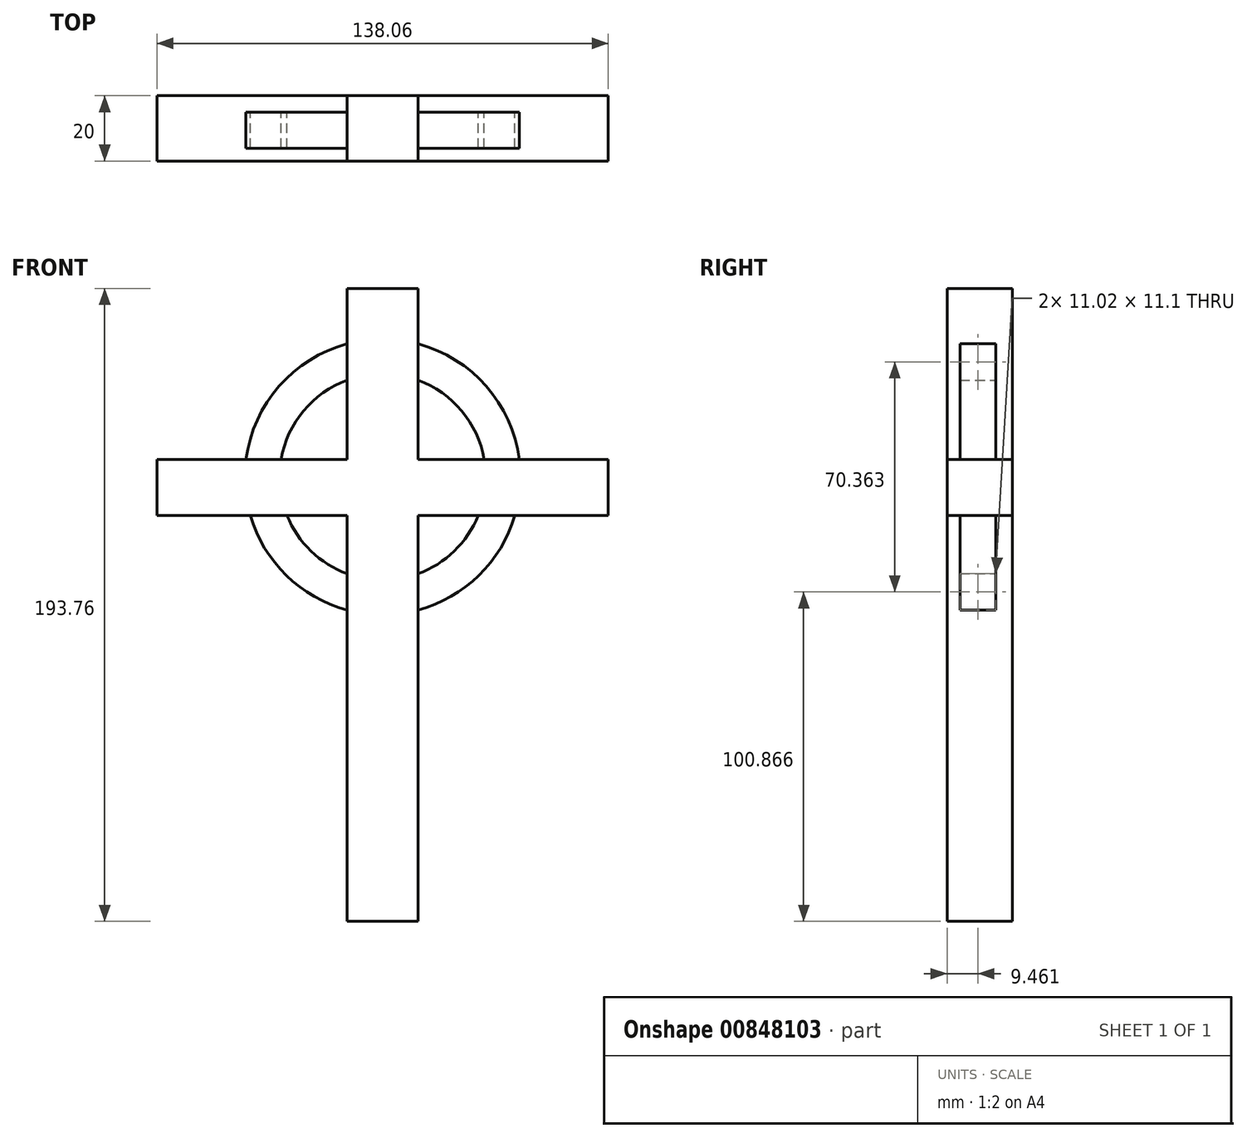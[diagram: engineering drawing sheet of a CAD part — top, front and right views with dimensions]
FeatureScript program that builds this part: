
annotation { "Feature Type Name" : "Feature", "Feature Type Description" : "" }
export const myFeature = defineFeature(function(context is Context, id is Id, definition is map)
    precondition{}
    {
        {
            var Q0;
            Q0=qCreatedBy(makeId("Front.planeOp"),FACE);
            var sketch = newSketch(context, id + "F0", { "sketchPlane" : qUnion([Q0])});
            skLineSegment(sketch, "E0.bottom", {"start": v(10.81, -96.88) * mm, "end": v(-10.81, -96.88) * mm});
            skLineSegment(sketch, "E0.top", {"start": v(10.81, 96.88) * mm, "end": v(-10.81, 96.88) * mm});
            skLineSegment(sketch, "E0.left", {"start": v(10.81, -96.88) * mm, "end": v(10.81, 96.88) * mm});
            skLineSegment(sketch, "E0.right", {"start": v(-10.81, -96.88) * mm, "end": v(-10.81, 96.88) * mm});
            skPoint(sketch, "E0.middle", {"position": v(0, 0) * mm});
            skLineSegment(sketch, "E1", {"start": v(0, 0) * mm, "end": v(0, 71.9) * mm, "construction": true});
            skLineSegment(sketch, "E2.bottom", {"start": v(69.03, 27.36) * mm, "end": v(-69.03, 27.36) * mm});
            skLineSegment(sketch, "E2.top", {"start": v(69.03, 44.54) * mm, "end": v(-69.03, 44.54) * mm});
            skLineSegment(sketch, "E2.left", {"start": v(69.03, 27.36) * mm, "end": v(69.03, 44.54) * mm});
            skLineSegment(sketch, "E2.right", {"start": v(-69.03, 27.36) * mm, "end": v(-69.03, 44.54) * mm});
            skPoint(sketch, "E2.middle", {"position": v(0, 35.95) * mm});
            skSolve(sketch);
        }
        {
            var Q0;
            Q0 = qSketchRegion(id + "F0", true);
            extrude(context, id + "F1", {"entities" : qUnion([Q0]), "depth" : 20 * mm, "offsetDistance" : 25.4 * mm});
        }
        {
            var Q0;
            Q0=qCreatedBy(makeId("Front.planeOp"),FACE);
            var sketch = newSketch(context, id + "F2", { "sketchPlane" : qUnion([Q0])});
            skLineSegment(sketch, "E3", {"start": v(0, 0) * mm, "end": v(0, 78.33) * mm, "construction": true});
            skCircle(sketch, "E4", {"center": v(0, 39.17) * mm, "radius": 42.14 * mm});
            skCircle(sketch, "E5", {"center": v(0, 39.17) * mm, "radius": 31.54 * mm});
            skSolve(sketch);
        }
        {
            var Q0;
            Q0 = qSketchRegion(id + "F2", true);
            extrude(context, id + "F3", {"entities" : qUnion([Q0]), "operationType" : NewBodyOperationType.ADD, "depth" : 16.05 * mm, "offsetDistance" : 25.4 * mm, "hasSecondDirection" : true, "secondDirectionOppositeDirection" : false, "secondDirectionDepth" : 5.03 * mm});
        }
    });
